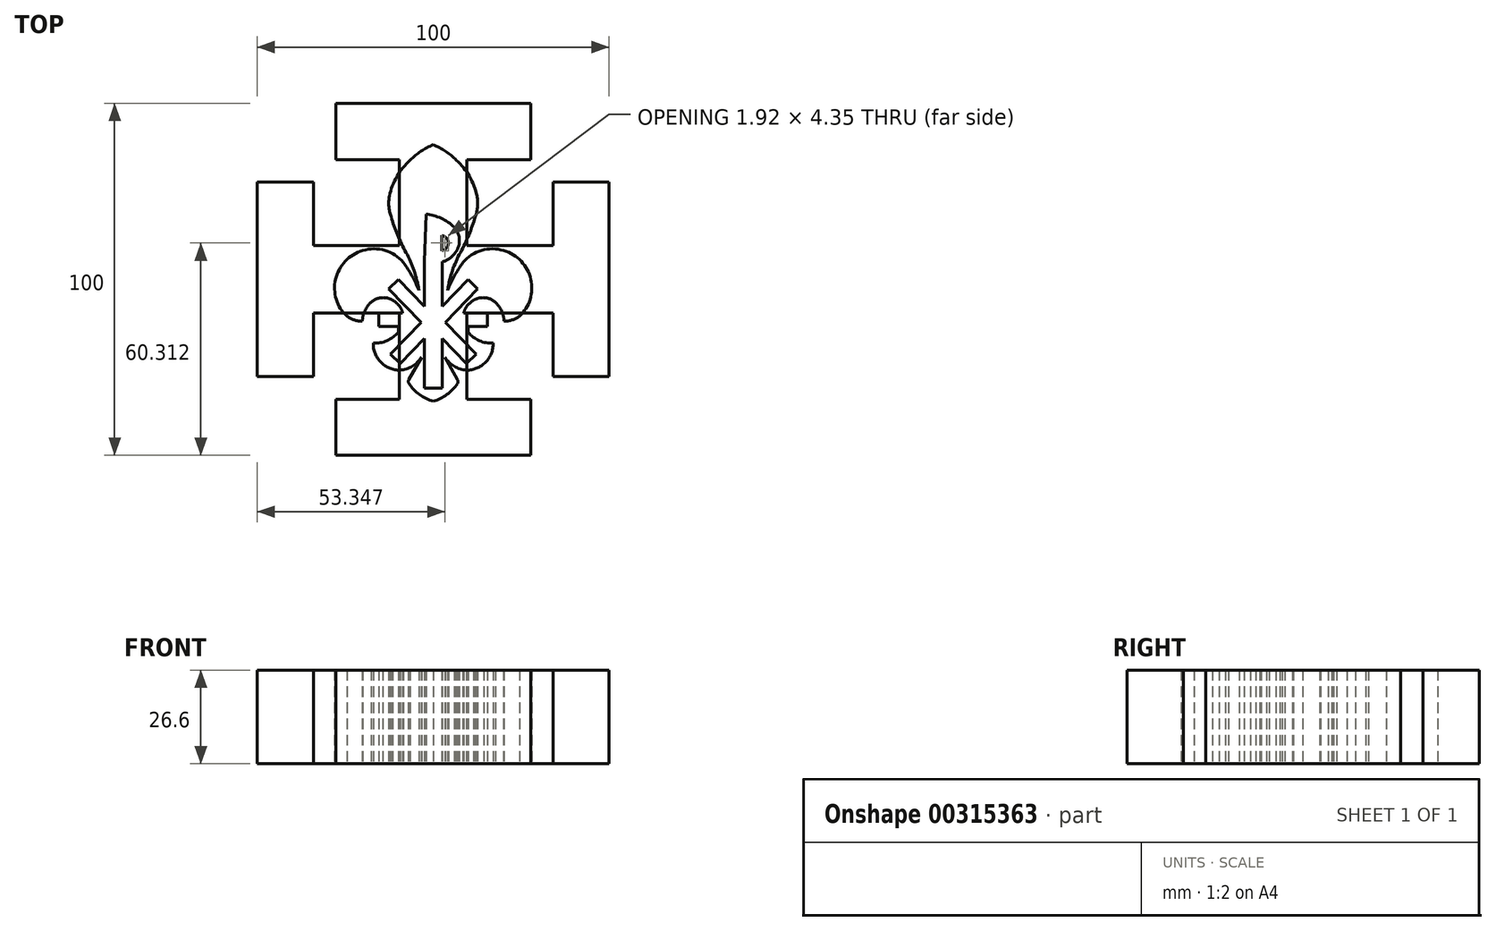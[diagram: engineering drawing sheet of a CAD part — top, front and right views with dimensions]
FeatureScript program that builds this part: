
annotation { "Feature Type Name" : "Feature", "Feature Type Description" : "" }
export const myFeature = defineFeature(function(context is Context, id is Id, definition is map)
    precondition{}
    {
        {
            var Q0;
            Q0=qCreatedBy(makeId("Top.planeOp"),FACE);
            var sketch = newSketch(context, id + "F0", { "sketchPlane" : qUnion([Q0])});
            skPoint(sketch, "E0", {"position": v(0, 0) * mm});
            skPoint(sketch, "E0.positionSnap0", {"position": v(-50, 0) * mm});
            skPoint(sketch, "E0.positionSnap1", {"position": v(0, 47.07) * mm});
            skSolve(sketch);
        }
        {
            var Q0;
            Q0=qCreatedBy(makeId("Top.planeOp"),FACE);
            var sketch = newSketch(context, id + "F1", { "sketchPlane" : qUnion([Q0])});
            skLineSegment(sketch, "E1", {"start": v(0, 59.83) * mm, "end": v(0, -42.42) * mm, "construction": true});
            skPoint(sketch, "E2", {"position": v(-10.4, 25.8) * mm});
            skPoint(sketch, "E3", {"position": v(-0.02, 35.95) * mm});
            skLineSegment(sketch, "E4", {"start": v(-10.4, 25.8) * mm, "end": v(-0.02, 35.95) * mm, "construction": true});
            skPoint(sketch, "E5", {"position": v(-5.2, 30.87) * mm});
            skPoint(sketch, "E6", {"position": v(-6.16, 31.84) * mm});
            skLineSegment(sketch, "E7", {"start": v(-6.16, 31.84) * mm, "end": v(-5.2, 30.87) * mm, "construction": true});
            skLineSegment(sketch, "E8", {"start": v(-10.4, 25.8) * mm, "end": v(-6.16, 31.84) * mm, "construction": true});
            skLineSegment(sketch, "E9", {"start": v(-0.02, 35.95) * mm, "end": v(-6.16, 31.84) * mm, "construction": true});
            skLineSegment(sketch, "E10", {"start": v(-3.09, 33.9) * mm, "end": v(7.9, 17.47) * mm, "construction": true});
            skLineSegment(sketch, "E11", {"start": v(-8.28, 28.82) * mm, "end": v(7.9, 17.47) * mm, "construction": true});
            skArc(sketch, "E12", {"start": v(0, 35.96) * mm, "mid": v(-3.27, 34.19) * mm, "end": v(-6.16, 31.84) * mm});
            skPoint(sketch, "E13", {"position": v(-11.7, 18.47) * mm});
            skPoint(sketch, "E14", {"position": v(-7.26, 7.17) * mm});
            skPoint(sketch, "E15", {"position": v(-3.83, -2.88) * mm});
            skPoint(sketch, "E16", {"position": v(-5, 1.95) * mm});
            skLineSegment(sketch, "E17", {"start": v(-11.7, 18.47) * mm, "end": v(-10.4, 25.8) * mm, "construction": true});
            skLineSegment(sketch, "E18", {"start": v(-11.05, 22.14) * mm, "end": v(-11.7, 22.25) * mm, "construction": true});
            skLineSegment(sketch, "E19", {"start": v(-11.7, 18.47) * mm, "end": v(-11.7, 22.25) * mm, "construction": true});
            skLineSegment(sketch, "E20", {"start": v(-10.4, 25.8) * mm, "end": v(-11.7, 22.25) * mm, "construction": true});
            skLineSegment(sketch, "E21", {"start": v(-11.7, 20.36) * mm, "end": v(-1.14, 20.36) * mm, "construction": true});
            skLineSegment(sketch, "E22", {"start": v(-11.05, 24.03) * mm, "end": v(-1.14, 20.36) * mm, "construction": true});
            skArc(sketch, "E23", {"start": v(-6.16, 31.84) * mm, "mid": v(-9.68, 27.48) * mm, "end": v(-11.7, 22.25) * mm});
            skArc(sketch, "E24.trimOffspring", {"start": v(-11.7, 22.25) * mm, "mid": v(-11.84, 19.46) * mm, "end": v(-11.24, 16.73) * mm});
            skArc(sketch, "E25", {"start": v(-11.24, 16.73) * mm, "mid": v(-9.52, 11.84) * mm, "end": v(-7.26, 7.17) * mm});
            skArc(sketch, "E26", {"start": v(-3.83, -2.88) * mm, "mid": v(-5.11, 2.3) * mm, "end": v(-7.26, 7.17) * mm});
            skArc(sketch, "E27", {"start": v(-3.83, -2.88) * mm, "mid": v(-5.66, 0.92) * mm, "end": v(-7.96, 4.45) * mm});
            skArc(sketch, "E28", {"start": v(-7.96, 4.45) * mm, "mid": v(-12.9, 7.74) * mm, "end": v(-18.82, 7.67) * mm});
            skArc(sketch, "E29", {"start": v(-18.82, 7.67) * mm, "mid": v(-23.5, 4.82) * mm, "end": v(-26.08, 0) * mm});
            skArc(sketch, "E30", {"start": v(-26.08, 0) * mm, "mid": v(-25.9, -5.33) * mm, "end": v(-23.04, -9.83) * mm});
            skArc(sketch, "E31", {"start": v(-23.04, -9.83) * mm, "mid": v(-21.1, -10.84) * mm, "end": v(-18.92, -11.16) * mm});
            skArc(sketch, "E32", {"start": v(-18.31, -8.52) * mm, "mid": v(-18.75, -9.8) * mm, "end": v(-18.92, -11.16) * mm});
            skArc(sketch, "E33", {"start": v(-13.47, -4.88) * mm, "mid": v(-15.17, -5.2) * mm, "end": v(-16.62, -6.15) * mm});
            skArc(sketch, "E34", {"start": v(-10.8, -5.56) * mm, "mid": v(-12.08, -5.03) * mm, "end": v(-13.47, -4.88) * mm});
            skArc(sketch, "E35", {"start": v(-8.17, -9) * mm, "mid": v(-8.46, -8.08) * mm, "end": v(-8.94, -7.24) * mm});
            skArc(sketch, "E36", {"start": v(-8.94, -7.24) * mm, "mid": v(-9.8, -6.33) * mm, "end": v(-10.8, -5.56) * mm});
            skArc(sketch, "E37", {"start": v(-16.62, -6.15) * mm, "mid": v(-17.59, -7.25) * mm, "end": v(-18.31, -8.52) * mm});
            skLineSegment(sketch, "E38", {"start": v(-14.5, -9) * mm, "end": v(-14.5, -12.62) * mm});
            skLineSegment(sketch, "E39", {"start": v(-14.5, -12.62) * mm, "end": v(-9.34, -12.62) * mm});
            skLineSegment(sketch, "E40", {"start": v(-9.34, -12.62) * mm, "end": v(-9.34, -14.11) * mm});
            skArc(sketch, "E41", {"start": v(-16.02, -17.03) * mm, "mid": v(-12.33, -16.38) * mm, "end": v(-9.34, -14.11) * mm});
            skArc(sketch, "E42", {"start": v(-16.02, -17.03) * mm, "mid": v(-13.98, -22.16) * mm, "end": v(-8.87, -24.25) * mm});
            skArc(sketch, "E43", {"start": v(-8.87, -24.25) * mm, "mid": v(-5.59, -23.2) * mm, "end": v(-3.13, -20.77) * mm});
            skLineSegment(sketch, "E44", {"start": v(-3.13, -20.77) * mm, "end": v(-6.5, -26.8) * mm});
            skArc(sketch, "E45", {"start": v(-6.47, -27.84) * mm, "mid": v(-3.67, -30.78) * mm, "end": v(0, -32.54) * mm});
            skPoint(sketch, "E46.visualSharp", {"position": v(-6.8, -27.31) * mm});
            skArc(sketch, "E46.filletArc", {"start": v(-6.5, -26.8) * mm, "mid": v(-6.64, -27.33) * mm, "end": v(-6.47, -27.84) * mm});
            skLineSegment(sketch, "E47", {"start": v(0, 35.96) * mm, "end": v(0, -32.54) * mm});
            skLineSegment(sketch, "E48", {"start": v(-14.5, -9) * mm, "end": v(-8.17, -9) * mm});
            skSolve(sketch);
        }
        {
            var Q0;
            Q0=qCreatedBy(makeId("Top.planeOp"),FACE);
            var sketch = newSketch(context, id + "F2", { "sketchPlane" : qUnion([Q0])});
            skPoint(sketch, "E49", {"position": v(-1.93, 17.4) * mm});
            skArc(sketch, "E50", {"start": v(5.6, 13.92) * mm, "mid": v(2.13, 16.3) * mm, "end": v(-1.93, 17.4) * mm});
            skArc(sketch, "E51", {"start": v(5.6, 6.73) * mm, "mid": v(6.99, 10.32) * mm, "end": v(5.6, 13.92) * mm});
            skArc(sketch, "E52", {"start": v(2.39, 4.68) * mm, "mid": v(4.17, 5.44) * mm, "end": v(5.6, 6.73) * mm});
            skLineSegment(sketch, "E53", {"start": v(2.39, 4.68) * mm, "end": v(2.39, -7.23) * mm});
            skLineSegment(sketch, "E54", {"start": v(2.39, -7.23) * mm, "end": v(9.3, -0.09) * mm});
            skLineSegment(sketch, "E55", {"start": v(3.23, -11.5) * mm, "end": v(11.88, -2.58) * mm});
            skLineSegment(sketch, "E56", {"start": v(11.88, -2.58) * mm, "end": v(9.3, -0.09) * mm});
            skLineSegment(sketch, "E57", {"start": v(3.23, -11.5) * mm, "end": v(37.65, -11.5) * mm, "construction": true});
            skLineSegment(sketch, "E58.MirrorCS", {"start": v(3.23, -11.5) * mm, "end": v(11.43, -19.96) * mm});
            skLineSegment(sketch, "E59.MirrorCS", {"start": v(2.39, -15.78) * mm, "end": v(8.86, -22.45) * mm});
            skLineSegment(sketch, "E60", {"start": v(11.43, -19.96) * mm, "end": v(8.86, -22.45) * mm});
            skLineSegment(sketch, "E61", {"start": v(2.39, -15.78) * mm, "end": v(2.39, -29.1) * mm});
            skLineSegment(sketch, "E62", {"start": v(2.39, -29.1) * mm, "end": v(0, -29.1) * mm});
            skLineSegment(sketch, "E63", {"start": v(0, -29.1) * mm, "end": v(0, 54.49) * mm, "construction": true});
            skLineSegment(sketch, "E64.MirrorCS", {"start": v(-3.23, -11.5) * mm, "end": v(-11.43, -19.96) * mm});
            skLineSegment(sketch, "E65.MirrorCS", {"start": v(-2.39, -15.78) * mm, "end": v(-8.86, -22.45) * mm});
            skLineSegment(sketch, "E66.MirrorCS", {"start": v(-11.43, -19.96) * mm, "end": v(-8.86, -22.45) * mm});
            skLineSegment(sketch, "E67.MirrorCS", {"start": v(-2.39, -7.23) * mm, "end": v(-9.3, -0.09) * mm});
            skLineSegment(sketch, "E68.MirrorCS", {"start": v(-3.23, -11.5) * mm, "end": v(-11.88, -2.58) * mm});
            skLineSegment(sketch, "E69.MirrorCS", {"start": v(-11.88, -2.58) * mm, "end": v(-9.3, -0.09) * mm});
            skLineSegment(sketch, "E70.MirrorCS", {"start": v(-2.39, -15.78) * mm, "end": v(-2.39, -29.1) * mm});
            skLineSegment(sketch, "E71.MirrorCS", {"start": v(-2.39, 4.68) * mm, "end": v(-2.39, -7.23) * mm});
            skLineSegment(sketch, "E72.MirrorCS", {"start": v(-2.39, -29.1) * mm, "end": v(0, -29.1) * mm});
            skLineSegment(sketch, "E73", {"start": v(-2.39, 4.68) * mm, "end": v(-1.93, 17.4) * mm});
            skLineSegment(sketch, "E74", {"start": v(2.24, 11.74) * mm, "end": v(2.24, 7.65) * mm});
            skArc(sketch, "E75", {"start": v(2.24, 7.65) * mm, "mid": v(4.05, 9.7) * mm, "end": v(2.24, 11.74) * mm});
            skSolve(sketch);
        }
        {
            var Q0;
            Q0=qCreatedBy(makeId("Top.planeOp"),FACE);
            var sketch = newSketch(context, id + "F3", { "sketchPlane" : qUnion([Q0])});
            skLineSegment(sketch, "E76", {"start": v(-47, 26) * mm, "end": v(-32, 26) * mm});
            skLineSegment(sketch, "E77", {"start": v(-32, 26) * mm, "end": v(-32, 9) * mm});
            skLineSegment(sketch, "E78", {"start": v(-32, 9) * mm, "end": v(-9, 9) * mm});
            skLineSegment(sketch, "E79", {"start": v(-47, 26) * mm, "end": v(-47, 0) * mm});
            skLineSegment(sketch, "E80", {"start": v(0, 0) * mm, "end": v(-37.51, 37.51) * mm, "construction": true});
            skLineSegment(sketch, "E81.MirrorCS", {"start": v(-26, 47) * mm, "end": v(0, 47) * mm});
            skLineSegment(sketch, "E82.MirrorCS", {"start": v(-26, 47) * mm, "end": v(-26, 32) * mm});
            skLineSegment(sketch, "E83.MirrorCS", {"start": v(-26, 32) * mm, "end": v(-9, 32) * mm});
            skLineSegment(sketch, "E84.MirrorCS", {"start": v(-9, 32) * mm, "end": v(-9, 9) * mm});
            skLineSegment(sketch, "E85.MirrorCS", {"start": v(26, 47) * mm, "end": v(0, 47) * mm});
            skLineSegment(sketch, "E86.MirrorCS", {"start": v(26, 47) * mm, "end": v(26, 32) * mm});
            skLineSegment(sketch, "E87.MirrorCS", {"start": v(26, 32) * mm, "end": v(9, 32) * mm});
            skLineSegment(sketch, "E88.MirrorCS", {"start": v(9, 32) * mm, "end": v(9, 9) * mm});
            skLineSegment(sketch, "E89.MirrorCS", {"start": v(32, 9) * mm, "end": v(9, 9) * mm});
            skLineSegment(sketch, "E90.MirrorCS", {"start": v(32, 26) * mm, "end": v(32, 9) * mm});
            skLineSegment(sketch, "E91.MirrorCS", {"start": v(47, 26) * mm, "end": v(32, 26) * mm});
            skLineSegment(sketch, "E92.MirrorCS", {"start": v(47, 26) * mm, "end": v(47, 0) * mm});
            skLineSegment(sketch, "E93.MirrorCS", {"start": v(-47, -26) * mm, "end": v(-47, 0) * mm});
            skLineSegment(sketch, "E94.MirrorCS", {"start": v(-47, -26) * mm, "end": v(-32, -26) * mm});
            skLineSegment(sketch, "E95.MirrorCS", {"start": v(-32, -26) * mm, "end": v(-32, -9) * mm});
            skLineSegment(sketch, "E96.MirrorCS", {"start": v(-32, -9) * mm, "end": v(-9, -9) * mm});
            skLineSegment(sketch, "E97.MirrorCS", {"start": v(-26, -47) * mm, "end": v(-26, -32) * mm});
            skLineSegment(sketch, "E98.MirrorCS", {"start": v(-26, -47) * mm, "end": v(0, -47) * mm});
            skLineSegment(sketch, "E99.MirrorCS", {"start": v(26, -47) * mm, "end": v(26, -32) * mm});
            skLineSegment(sketch, "E100.MirrorCS", {"start": v(26, -32) * mm, "end": v(9, -32) * mm});
            skLineSegment(sketch, "E101.MirrorCS", {"start": v(9, -32) * mm, "end": v(9, -9) * mm});
            skLineSegment(sketch, "E102.MirrorCS", {"start": v(32, -9) * mm, "end": v(9, -9) * mm});
            skLineSegment(sketch, "E103.MirrorCS", {"start": v(47, -26) * mm, "end": v(47, 0) * mm});
            skLineSegment(sketch, "E104.MirrorCS", {"start": v(47, -26) * mm, "end": v(32, -26) * mm});
            skLineSegment(sketch, "E105.MirrorCS", {"start": v(32, -26) * mm, "end": v(32, -9) * mm});
            skLineSegment(sketch, "E106.MirrorCS", {"start": v(-26, -32) * mm, "end": v(-9, -32) * mm});
            skLineSegment(sketch, "E107.MirrorCS", {"start": v(-9, -32) * mm, "end": v(-9, -9) * mm});
            skLineSegment(sketch, "E108.MirrorCS", {"start": v(26, -47) * mm, "end": v(0, -47) * mm});
            skSolve(sketch);
        }
        {
            var Q0;
            Q0=makeQuery(id+"F1.imprint","IMPRINT",FACE,{"disambiguationData":[TD([[makeQuery(id+"F1.imprint","IMPRINT",EDGE,{"derivedFrom":sQuery(id+"F1.wireOp",EDGE,"E12")}),1.0]])]});
            extrude(context, id + "F4", {"entities" : qUnion([Q0]), "depth" : 25 * mm, "offsetDistance" : 25 * mm});
        }
        {
            var Q0;
            Q0=makeQuery(id+"F4.opExtrude","SWEPT_BODY",BODY,{"disambiguationData":[OSD([sQuery(id+"F1.wireOp",EDGE,"E12"),sQuery(id+"F1.wireOp",EDGE,"E23"),sQuery(id+"F1.wireOp",EDGE,"E24.trimOffspring"),sQuery(id+"F1.wireOp",EDGE,"E25"),sQuery(id+"F1.wireOp",EDGE,"E26"),sQuery(id+"F1.wireOp",EDGE,"E27"),sQuery(id+"F1.wireOp",EDGE,"E28"),sQuery(id+"F1.wireOp",EDGE,"E29"),sQuery(id+"F1.wireOp",EDGE,"E30"),sQuery(id+"F1.wireOp",EDGE,"E31"),sQuery(id+"F1.wireOp",EDGE,"E32"),sQuery(id+"F1.wireOp",EDGE,"E33"),sQuery(id+"F1.wireOp",EDGE,"E34"),sQuery(id+"F1.wireOp",EDGE,"E35"),sQuery(id+"F1.wireOp",EDGE,"E36"),sQuery(id+"F1.wireOp",EDGE,"E37"),sQuery(id+"F1.wireOp",EDGE,"E38"),sQuery(id+"F1.wireOp",EDGE,"E39"),sQuery(id+"F1.wireOp",EDGE,"E40"),sQuery(id+"F1.wireOp",EDGE,"E41"),sQuery(id+"F1.wireOp",EDGE,"E42"),sQuery(id+"F1.wireOp",EDGE,"E43"),sQuery(id+"F1.wireOp",EDGE,"E44"),sQuery(id+"F1.wireOp",EDGE,"E45"),sQuery(id+"F1.wireOp",EDGE,"E46.filletArc"),sQuery(id+"F1.wireOp",EDGE,"E47"),sQuery(id+"F1.wireOp",EDGE,"E48")])]});
            var Q1;
            Q1=makeQuery(id+"F4.opExtrude","SWEPT_FACE",FACE,{"disambiguationData":[OSD([sQuery(id+"F1.wireOp",EDGE,"E47")])]});
            mirror(context, id + "F5", {"operationType" : NewBodyOperationType.ADD, "entities" : qUnion([Q0]), "mirrorPlane" : qUnion([Q1])});
        }
        {
            var Q0;
            Q0=makeQuery(id+"F2.imprint","IMPRINT",FACE,{"disambiguationData":[TD([[makeQuery(id+"F2.imprint","IMPRINT",EDGE,{"derivedFrom":sQuery(id+"F2.wireOp",EDGE,"E50")}),1.0]])]});
            extrude(context, id + "F6", {"entities" : qUnion([Q0]), "depth" : 25 * mm, "offsetDistance" : 25 * mm});
        }
        {
            var Q0;
            Q0=makeQuery(id+"F3.imprint","IMPRINT",FACE,{"disambiguationData":[TD([[makeQuery(id+"F3.imprint","IMPRINT",EDGE,{"derivedFrom":sQuery(id+"F3.wireOp",EDGE,"E76")}),-1.0]])]});
            extrude(context, id + "F7", {"entities" : qUnion([Q0]), "depth" : 25 * mm, "offsetDistance" : 25 * mm});
        }
        {
            var Q0;
            Q0=makeQuery(id+"F4.opExtrude","SWEPT_BODY",BODY,{"disambiguationData":[OSD([sQuery(id+"F1.wireOp",EDGE,"E12"),sQuery(id+"F1.wireOp",EDGE,"E23"),sQuery(id+"F1.wireOp",EDGE,"E24.trimOffspring"),sQuery(id+"F1.wireOp",EDGE,"E25"),sQuery(id+"F1.wireOp",EDGE,"E26"),sQuery(id+"F1.wireOp",EDGE,"E27"),sQuery(id+"F1.wireOp",EDGE,"E28"),sQuery(id+"F1.wireOp",EDGE,"E29"),sQuery(id+"F1.wireOp",EDGE,"E30"),sQuery(id+"F1.wireOp",EDGE,"E31"),sQuery(id+"F1.wireOp",EDGE,"E32"),sQuery(id+"F1.wireOp",EDGE,"E33"),sQuery(id+"F1.wireOp",EDGE,"E34"),sQuery(id+"F1.wireOp",EDGE,"E35"),sQuery(id+"F1.wireOp",EDGE,"E36"),sQuery(id+"F1.wireOp",EDGE,"E37"),sQuery(id+"F1.wireOp",EDGE,"E38"),sQuery(id+"F1.wireOp",EDGE,"E39"),sQuery(id+"F1.wireOp",EDGE,"E40"),sQuery(id+"F1.wireOp",EDGE,"E41"),sQuery(id+"F1.wireOp",EDGE,"E42"),sQuery(id+"F1.wireOp",EDGE,"E43"),sQuery(id+"F1.wireOp",EDGE,"E44"),sQuery(id+"F1.wireOp",EDGE,"E45"),sQuery(id+"F1.wireOp",EDGE,"E46.filletArc"),sQuery(id+"F1.wireOp",EDGE,"E47"),sQuery(id+"F1.wireOp",EDGE,"E48")])]});
            var Q1;
            Q1=makeQuery(id+"F6.opExtrude","SWEPT_BODY",BODY,{"disambiguationData":[OSD([sQuery(id+"F2.wireOp",EDGE,"E50"),sQuery(id+"F2.wireOp",EDGE,"E51"),sQuery(id+"F2.wireOp",EDGE,"E52"),sQuery(id+"F2.wireOp",EDGE,"E53"),sQuery(id+"F2.wireOp",EDGE,"E54"),sQuery(id+"F2.wireOp",EDGE,"E55"),sQuery(id+"F2.wireOp",EDGE,"E56"),sQuery(id+"F2.wireOp",EDGE,"E58.MirrorCS"),sQuery(id+"F2.wireOp",EDGE,"E59.MirrorCS"),sQuery(id+"F2.wireOp",EDGE,"E60"),sQuery(id+"F2.wireOp",EDGE,"E61"),sQuery(id+"F2.wireOp",EDGE,"E62"),sQuery(id+"F2.wireOp",EDGE,"E64.MirrorCS"),sQuery(id+"F2.wireOp",EDGE,"E65.MirrorCS"),sQuery(id+"F2.wireOp",EDGE,"E66.MirrorCS"),sQuery(id+"F2.wireOp",EDGE,"E67.MirrorCS"),sQuery(id+"F2.wireOp",EDGE,"E68.MirrorCS"),sQuery(id+"F2.wireOp",EDGE,"E69.MirrorCS"),sQuery(id+"F2.wireOp",EDGE,"E70.MirrorCS"),sQuery(id+"F2.wireOp",EDGE,"E71.MirrorCS"),sQuery(id+"F2.wireOp",EDGE,"E72.MirrorCS"),sQuery(id+"F2.wireOp",EDGE,"E73"),sQuery(id+"F2.wireOp",EDGE,"E74"),sQuery(id+"F2.wireOp",EDGE,"E75")])]});
            var Q2;
            Q2=makeQuery(id+"F7.opExtrude","SWEPT_BODY",BODY,{"disambiguationData":[OSD([sQuery(id+"F3.wireOp",EDGE,"E76"),sQuery(id+"F3.wireOp",EDGE,"E77"),sQuery(id+"F3.wireOp",EDGE,"E78"),sQuery(id+"F3.wireOp",EDGE,"E79"),sQuery(id+"F3.wireOp",EDGE,"E81.MirrorCS"),sQuery(id+"F3.wireOp",EDGE,"E82.MirrorCS"),sQuery(id+"F3.wireOp",EDGE,"E83.MirrorCS"),sQuery(id+"F3.wireOp",EDGE,"E84.MirrorCS"),sQuery(id+"F3.wireOp",EDGE,"E85.MirrorCS"),sQuery(id+"F3.wireOp",EDGE,"E86.MirrorCS"),sQuery(id+"F3.wireOp",EDGE,"E87.MirrorCS"),sQuery(id+"F3.wireOp",EDGE,"E88.MirrorCS"),sQuery(id+"F3.wireOp",EDGE,"E89.MirrorCS"),sQuery(id+"F3.wireOp",EDGE,"E90.MirrorCS"),sQuery(id+"F3.wireOp",EDGE,"E91.MirrorCS"),sQuery(id+"F3.wireOp",EDGE,"E92.MirrorCS"),sQuery(id+"F3.wireOp",EDGE,"E93.MirrorCS"),sQuery(id+"F3.wireOp",EDGE,"E94.MirrorCS"),sQuery(id+"F3.wireOp",EDGE,"E95.MirrorCS"),sQuery(id+"F3.wireOp",EDGE,"E96.MirrorCS"),sQuery(id+"F3.wireOp",EDGE,"E97.MirrorCS"),sQuery(id+"F3.wireOp",EDGE,"E98.MirrorCS"),sQuery(id+"F3.wireOp",EDGE,"E99.MirrorCS"),sQuery(id+"F3.wireOp",EDGE,"E100.MirrorCS"),sQuery(id+"F3.wireOp",EDGE,"E101.MirrorCS"),sQuery(id+"F3.wireOp",EDGE,"E102.MirrorCS"),sQuery(id+"F3.wireOp",EDGE,"E103.MirrorCS"),sQuery(id+"F3.wireOp",EDGE,"E104.MirrorCS"),sQuery(id+"F3.wireOp",EDGE,"E105.MirrorCS"),sQuery(id+"F3.wireOp",EDGE,"E106.MirrorCS"),sQuery(id+"F3.wireOp",EDGE,"E107.MirrorCS"),sQuery(id+"F3.wireOp",EDGE,"E108.MirrorCS")])]});
            var Q3;
            Q3=qCreatedBy(makeId("Origin.pointOp"),VERTEX);
            transform(context, id + "F8", {"entities" : qUnion([Q0, Q1, Q2]), "transformType" : TransformType.SCALE_UNIFORMLY, "scale" : 1.06, "scalePoint" : qUnion([Q3]), "makeCopy" : false});
        }
    });
